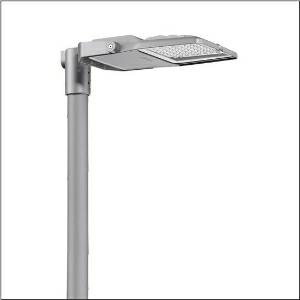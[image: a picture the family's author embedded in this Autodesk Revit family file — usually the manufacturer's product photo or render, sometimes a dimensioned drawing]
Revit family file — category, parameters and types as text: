
# Revit family: floodlight_fl_21_mini___pl52_5xa7776c2d3a_1d2c
name_source: partatom
category: Lighting Fixtures
units: mm (PartAtom-declared; Revit-internal decimal feet)

## family parameters
Cut with Voids When Loaded = No
Host = Face
Light Source = No
Part Type = Normal
Room Calculation Point = No
Round Connector Dimension = Use Diameter
Shared = No

## types (1)
- --- (1 x LED, 12190 lm, 89 W, 3000K)
    Apparent Load = 89 VA
    CIE Flux Codes = 26 60 98 100 100
    Color Rendering = 70
    Color Temperature = 3000K
    Default Elevation = 1800 mm
    Description = Floodlight FL 21 mini, floodlight, primary light control with lens, of PMMA, primary optical cover: protective disc, of toughened safety glass, transparent, light distribution: PL52, light emission: direct distribution, installation type: surface-mounted, LED, High Power LED, rated luminous flux: 12.190lm, luminous efficacy: 137lm/W, light colour: 730, colour temperature: 3000K, control gear: ECG Smart Interface, control: flexible luminous flux parameterisation, time-dependent luminous flux control, constant luminous flux control, overheat protection, presetting dimming logarithmic, with terminal, 6-pole, mains connection: 220..240V, AC, 50/60Hz, start of lifetime: 89W, end of lifetime: 94W, reduction: 43W, luminaire housing, of diecast aluminium, powder-coated, Siteco® metallic grey (DB 702S), corrosivity category C5 according to DIN EN ISO 12944, mast bracket, of steel, galvanised, powder-coated, Siteco® metallic grey (DB 702S), protection rating (complete): IP66, insulation class (complete): insulation class II (safety insulation), certification: CE, protection symbol: D, impact resistance: IK08, permissible operating ambient temperature: -40..+40°C, permissible operating ambient temperature for outdoor applications: -40..+50°C, standard: DIN EN 12944, packaging unit: 1 piece

Light Distribution: PL52
    Height = 70 mm
    Lamp = 1 x LED
    Lamp Light Flux = 12190 lm
    Lamp Power = 89 W
    Lamp count = 1
    Length = 485 mm
    Luminous efficacy = 137 lm/W
    Manufacturer = Siteco
    ModVariant = No
    Model = 5XA7776C2D3A
    Number of Poles = 1
    OnlyDefault = Yes
    Power Factor = 1
    Product Name = Floodlight FL 21 mini | PL52
    Product group = floodlight | pylon top
    ProductGroupID = 6101
    Protection Class = Protection class II
    Protection Degree = IP 66
    RLX_Detail_Level = 1
    RlxData = <blob elided: 100777 chars, md5=de9fc450>
    Socket = socket
    Standby Power = 0 W
    System Light Flux = 12190 lm
    System Power = 89 W
    Type Comments = factory setting: luminous flux: 100 % | dim-lin: 254 | 456 mA
    Type Image = l_1007125.jpg
    URL = http://relux.com
    VarID = @adj_074445
    Voltage = 0 V
    Weight = 0.00 kg
    Width = 337 mm

## geometry (parser evidence)
native form markers: Blend x4, Sweep x15
no freeform markers — native parametric forms only
